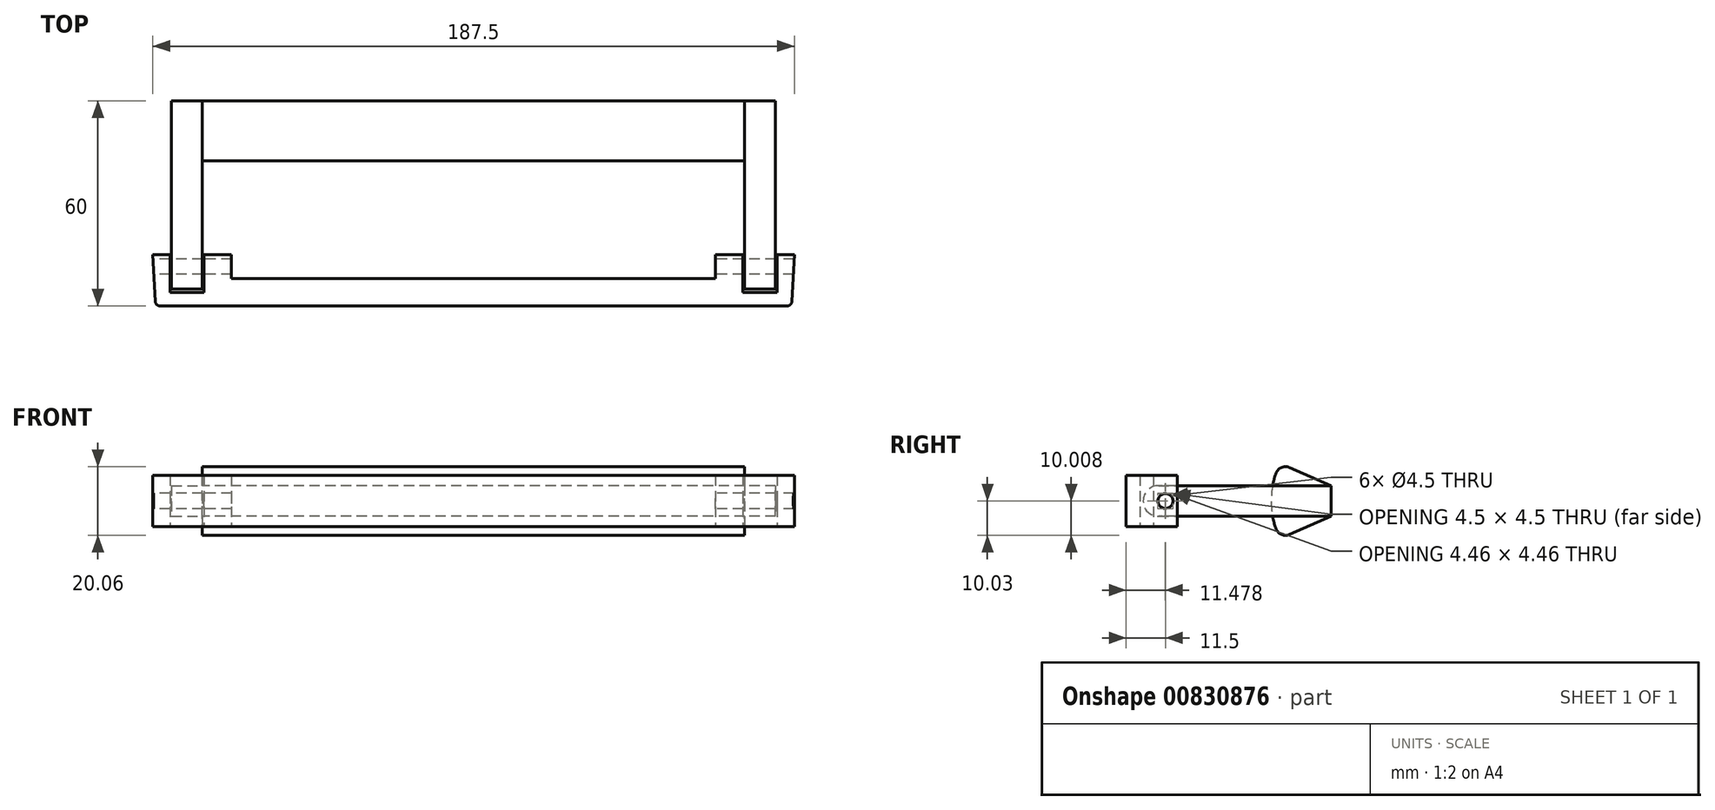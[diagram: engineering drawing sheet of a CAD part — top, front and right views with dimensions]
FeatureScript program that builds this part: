
annotation { "Feature Type Name" : "Feature", "Feature Type Description" : "" }
export const myFeature = defineFeature(function(context is Context, id is Id, definition is map)
    precondition{}
    {
        {
            var Q0;
            Q0=qCreatedBy(makeId("Top.planeOp"),FACE);
            var sketch = newSketch(context, id + "F0", { "sketchPlane" : qUnion([Q0])});
            skLineSegment(sketch, "E0", {"start": v(-93, 0) * mm, "end": v(93, 0) * mm});
            skLineSegment(sketch, "E1", {"start": v(93, 0) * mm, "end": v(93.75, 15) * mm});
            skLineSegment(sketch, "E2", {"start": v(93.75, 15) * mm, "end": v(88.75, 15) * mm});
            skLineSegment(sketch, "E3", {"start": v(88.75, 15) * mm, "end": v(88.75, 4) * mm});
            skLineSegment(sketch, "E4", {"start": v(88.75, 4) * mm, "end": v(78.75, 4) * mm});
            skLineSegment(sketch, "E5", {"start": v(78.75, 4) * mm, "end": v(78.75, 15) * mm});
            skLineSegment(sketch, "E6", {"start": v(78.75, 15) * mm, "end": v(70.75, 15) * mm});
            skLineSegment(sketch, "E7", {"start": v(70.75, 15) * mm, "end": v(70.75, 8) * mm});
            skLineSegment(sketch, "E8", {"start": v(70.75, 8) * mm, "end": v(-70.75, 8) * mm});
            skLineSegment(sketch, "E9", {"start": v(-70.75, 8) * mm, "end": v(-70.75, 15) * mm});
            skLineSegment(sketch, "E10", {"start": v(-70.75, 15) * mm, "end": v(-78.75, 15) * mm});
            skLineSegment(sketch, "E11", {"start": v(-78.75, 15) * mm, "end": v(-78.75, 4) * mm});
            skLineSegment(sketch, "E12", {"start": v(-78.75, 4) * mm, "end": v(-88.75, 4) * mm});
            skLineSegment(sketch, "E13", {"start": v(-88.75, 4) * mm, "end": v(-88.75, 15) * mm});
            skLineSegment(sketch, "E14", {"start": v(-88.75, 15) * mm, "end": v(-93.75, 15) * mm});
            skLineSegment(sketch, "E15", {"start": v(-93.75, 15) * mm, "end": v(-93, 0) * mm});
            skSolve(sketch);
        }
        {
            var Q0;
            Q0=makeQuery(id+"F0.imprint","IMPRINT",FACE,{"disambiguationData":[TD([[makeQuery(id+"F0.imprint","IMPRINT",EDGE,{"derivedFrom":sQuery(id+"F0.wireOp",EDGE,"E0")}),1.0]])]});
            extrude(context, id + "F1", {"entities" : qUnion([Q0]), "endBound" : BoundingType.SYMMETRIC, "depth" : 15 * mm, "offsetDistance" : 25 * mm});
        }
        {
            var Q0;
            Q0=qCreatedBy(makeId("Top.planeOp"),FACE);
            var sketch = newSketch(context, id + "F2", { "sketchPlane" : qUnion([Q0])});
            skLineSegment(sketch, "E16", {"start": v(79.25, 5) * mm, "end": v(88.25, 5) * mm});
            skLineSegment(sketch, "E17", {"start": v(88.25, 5) * mm, "end": v(88.25, 60) * mm});
            skLineSegment(sketch, "E18", {"start": v(88.25, 60) * mm, "end": v(-88.25, 60) * mm});
            skLineSegment(sketch, "E19", {"start": v(-88.25, 60) * mm, "end": v(-88.25, 5) * mm});
            skLineSegment(sketch, "E20", {"start": v(-88.25, 5) * mm, "end": v(-79.25, 5) * mm});
            skLineSegment(sketch, "E21", {"start": v(-79.25, 5) * mm, "end": v(-79.25, 45) * mm});
            skLineSegment(sketch, "E22", {"start": v(-79.25, 45) * mm, "end": v(79.25, 45) * mm});
            skLineSegment(sketch, "E23", {"start": v(79.25, 45) * mm, "end": v(79.25, 5) * mm});
            skSolve(sketch);
        }
        {
            var Q0;
            Q0 = qSketchRegion(id + "F2", true);
            extrude(context, id + "F3", {"entities" : qUnion([Q0]), "endBound" : BoundingType.SYMMETRIC, "depth" : 9 * mm, "offsetDistance" : 25 * mm});
        }
        {
            var Q0;
            Q0=makeQuery(id+"F1.opExtrude","SWEPT_FACE",FACE,{"disambiguationData":[OSD([sQuery(id+"F0.wireOp",EDGE,"E7")])]});
            var sketch = newSketch(context, id + "F4", { "sketchPlane" : qUnion([Q0])});
            skCircle(sketch, "E24", {"center": v(-11.5, 0) * mm, "radius": 2.25 * mm});
            skPoint(sketch, "E24.centerSnap0", {"position": v(-15, 0) * mm});
            skPoint(sketch, "E24.centerSnap1", {"position": v(-11.5, 7.5) * mm});
            skSolve(sketch);
        }
        {
            var Q0;
            Q0 = qSketchRegion(id + "F4", true);
            extrude(context, id + "F5", {"entities" : qUnion([Q0]), "operationType" : NewBodyOperationType.REMOVE, "endBound" : BoundingType.SYMMETRIC, "oppositeDirection" : true, "depth" : 500 * mm, "offsetDistance" : 25 * mm});
        }
        {
            var Q0;
            Q0=makeQuery(id+"F3.opExtrude","SWEPT_FACE",FACE,{"disambiguationData":[OSD([sQuery(id+"F2.wireOp",EDGE,"E21")])]});
            var sketch = newSketch(context, id + "F6", { "sketchPlane" : qUnion([Q0])});
            skLineSegment(sketch, "E25", {"start": v(45, 11) * mm, "end": v(45, -11) * mm});
            skLineSegment(sketch, "E26", {"start": v(45, -11) * mm, "end": v(60, -4.5) * mm});
            skLineSegment(sketch, "E27", {"start": v(60, -4.5) * mm, "end": v(60, 4.5) * mm});
            skLineSegment(sketch, "E28", {"start": v(60, 4.5) * mm, "end": v(45, 11) * mm});
            skArc(sketch, "E29", {"start": v(45, 11) * mm, "mid": v(42.45, 0) * mm, "end": v(45, -11) * mm});
            skSolve(sketch);
        }
        {
            var Q0;
            Q0 = qSketchRegion(id + "F6", true);
            var Q1;
            Q1=makeQuery(id+"F3.opExtrude","SWEPT_FACE",FACE,{"disambiguationData":[OSD([sQuery(id+"F2.wireOp",EDGE,"E23")])]});
            extrude(context, id + "F7", {"entities" : qUnion([Q0]), "operationType" : NewBodyOperationType.ADD, "endBound" : BoundingType.UP_TO_SURFACE, "depth" : 25 * mm, "endBoundEntityFace" : qUnion([Q1]), "offsetDistance" : 25 * mm});
        }
        {
            var Q0;
            Q0=makeQuery(id+"F3.opExtrude","CAP_EDGE",EDGE,{"disambiguationData":[OSD([sQuery(id+"F2.wireOp",EDGE,"E16")])],"isStart":false});
            var Q1;
            Q1=makeQuery(id+"F3.opExtrude","CAP_EDGE",EDGE,{"disambiguationData":[OSD([sQuery(id+"F2.wireOp",EDGE,"E16")])],"isStart":true});
            var Q2;
            Q2=makeQuery(id+"F3.opExtrude","CAP_EDGE",EDGE,{"disambiguationData":[OSD([sQuery(id+"F2.wireOp",EDGE,"E20")])],"isStart":true});
            var Q3;
            Q3=makeQuery(id+"F3.opExtrude","CAP_EDGE",EDGE,{"disambiguationData":[OSD([sQuery(id+"F2.wireOp",EDGE,"E20")])],"isStart":false});
            fillet(context, id + "F8", {"entities" : qUnion([Q0, Q1, Q2, Q3]), "radius" : 4.5 * mm, "tangentPropagation" : true, "allowEdgeOverflow" : false});
        }
        {
            var Q0;
            Q0=makeQuery(id+"F1.opExtrude","SWEPT_EDGE",EDGE,{"disambiguationData":[OSD([sQuery(id+"F0.wireOp",EDGE,"E0"),sQuery(id+"F0.wireOp",EDGE,"E1")])]});
            var Q1;
            Q1=makeQuery(id+"F1.opExtrude","SWEPT_EDGE",EDGE,{"disambiguationData":[OSD([sQuery(id+"F0.wireOp",EDGE,"E0"),sQuery(id+"F0.wireOp",EDGE,"E15")])]});
            var Q2;
            Q2=makeQuery(id+"F3.opExtrude","CAP_EDGE",EDGE,{"disambiguationData":[OSD([sQuery(id+"F2.wireOp",EDGE,"E17")])],"isStart":false});
            var Q3;
            Q3=makeQuery(id+"F3.opExtrude","CAP_EDGE",EDGE,{"disambiguationData":[OSD([sQuery(id+"F2.wireOp",EDGE,"E17")])],"isStart":true});
            var Q4;
            Q4=makeQuery(id+"F3.opExtrude","CAP_EDGE",EDGE,{"disambiguationData":[OSD([sQuery(id+"F2.wireOp",EDGE,"E19")])],"isStart":false});
            var Q5;
            Q5=makeQuery(id+"F3.opExtrude","CAP_EDGE",EDGE,{"disambiguationData":[OSD([sQuery(id+"F2.wireOp",EDGE,"E19")])],"isStart":true});
            var Q6;
            Q6=makeQuery(id+"F3.opExtrude","CAP_EDGE",EDGE,{"disambiguationData":[OSD([sQuery(id+"F2.wireOp",EDGE,"E23")])],"isStart":true});
            var Q7;
            Q7=makeQuery(id+"F3.opExtrude","CAP_EDGE",EDGE,{"disambiguationData":[OSD([sQuery(id+"F2.wireOp",EDGE,"E23")])],"isStart":false});
            var Q8;
            Q8=makeQuery(id+"F3.opExtrude","CAP_EDGE",EDGE,{"disambiguationData":[OSD([sQuery(id+"F2.wireOp",EDGE,"E21")])],"isStart":true});
            var Q9;
            Q9=makeQuery(id+"F3.opExtrude","CAP_EDGE",EDGE,{"disambiguationData":[OSD([sQuery(id+"F2.wireOp",EDGE,"E21")])],"isStart":false});
            var Q10;
            Q10=makeQuery(id+"F3.opExtrude","SWEPT_EDGE",EDGE,{"disambiguationData":[OSD([sQuery(id+"F2.wireOp",EDGE,"E18"),sQuery(id+"F2.wireOp",EDGE,"E19")])]});
            var Q11;
            Q11=makeQuery(id+"F7.boolean.opBoolean","MERGE",EDGE,{"derivedFrom":[makeQuery(id+"F3.opExtrude","CAP_EDGE",EDGE,{"disambiguationData":[OSD([sQuery(id+"F2.wireOp",EDGE,"E18")])],"isStart":false}),makeQuery(id+"F7.opExtrude","SWEPT_EDGE",EDGE,{"disambiguationData":[OSD([sQuery(id+"F6.wireOp",EDGE,"E27"),sQuery(id+"F6.wireOp",EDGE,"E28")])]})]});
            var Q12;
            Q12=makeQuery(id+"F7.boolean.opBoolean","MERGE",EDGE,{"derivedFrom":[makeQuery(id+"F3.opExtrude","CAP_EDGE",EDGE,{"disambiguationData":[OSD([sQuery(id+"F2.wireOp",EDGE,"E18")])],"isStart":true}),makeQuery(id+"F7.opExtrude","SWEPT_EDGE",EDGE,{"disambiguationData":[OSD([sQuery(id+"F6.wireOp",EDGE,"E26"),sQuery(id+"F6.wireOp",EDGE,"E27")])]})]});
            var Q13;
            Q13=makeQuery(id+"F3.opExtrude","SWEPT_EDGE",EDGE,{"disambiguationData":[OSD([sQuery(id+"F2.wireOp",EDGE,"E17"),sQuery(id+"F2.wireOp",EDGE,"E18")])]});
            fillet(context, id + "F9", {"entities" : qUnion([Q0, Q1, Q2, Q3, Q4, Q5, Q6, Q7, Q8, Q9, Q10, Q11, Q12, Q13]), "radius" : 1.5 * mm, "tangentPropagation" : true, "allowEdgeOverflow" : false});
        }
        {
            var Q0;
            Q0=makeQuery(id+"F7.opExtrude","SWEPT_EDGE",EDGE,{"disambiguationData":[OSD([sQuery(id+"F6.wireOp",EDGE,"E25"),sQuery(id+"F6.wireOp",EDGE,"E28")])]});
            var Q1;
            Q1=makeQuery(id+"F7.opExtrude","SWEPT_EDGE",EDGE,{"disambiguationData":[OSD([sQuery(id+"F6.wireOp",EDGE,"E25"),sQuery(id+"F6.wireOp",EDGE,"E26")])]});
            fillet(context, id + "F10", {"entities" : qUnion([Q0, Q1]), "radius" : 3 * mm, "tangentPropagation" : true, "allowEdgeOverflow" : false});
        }
    });
